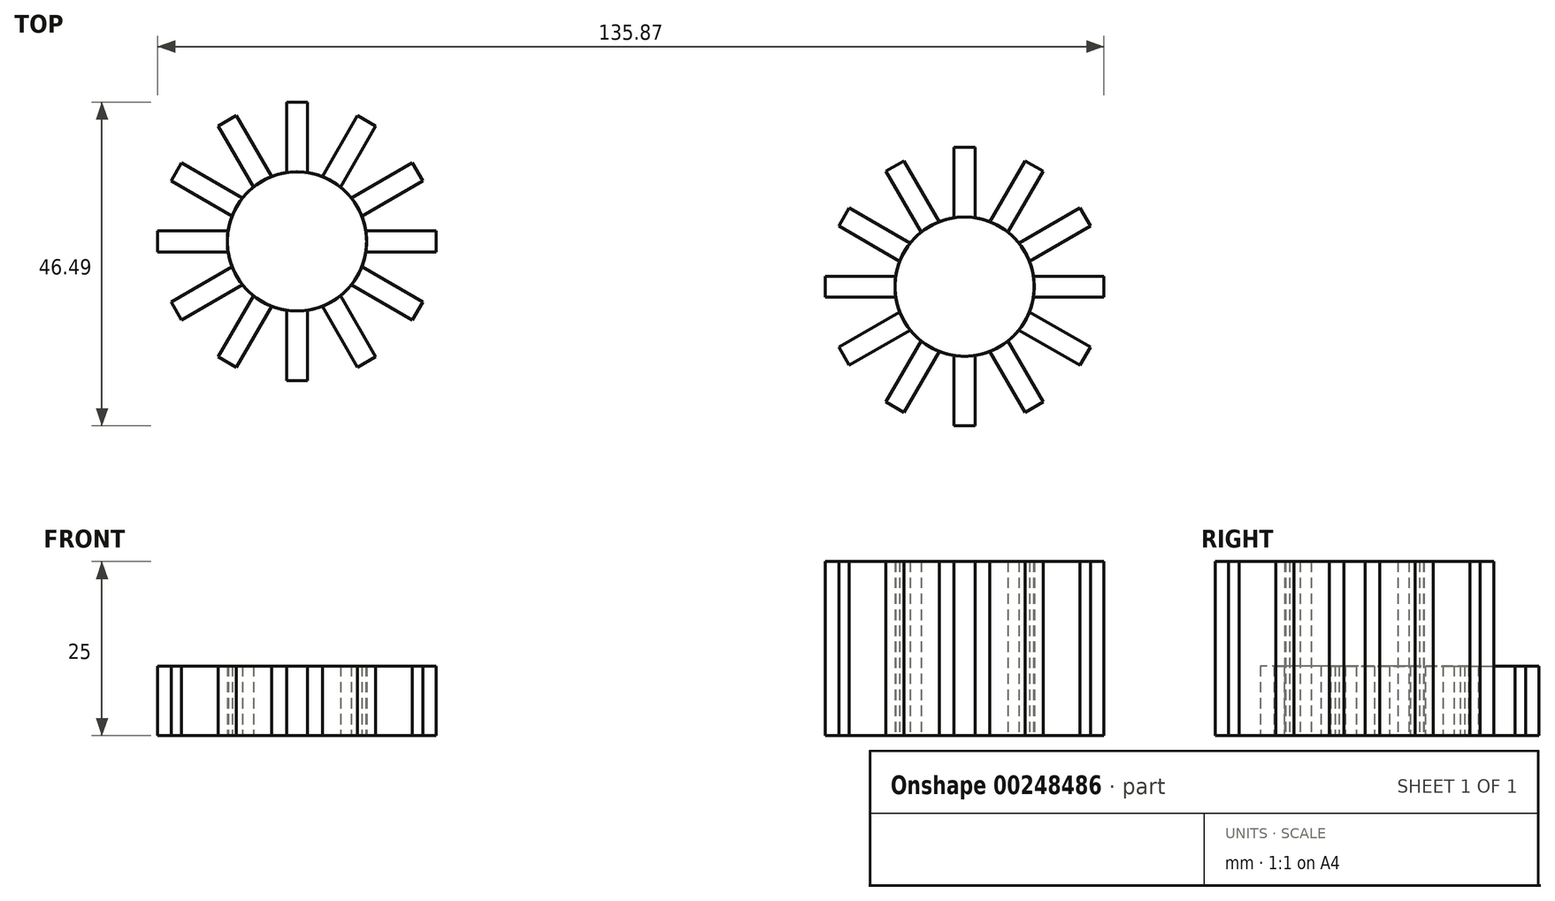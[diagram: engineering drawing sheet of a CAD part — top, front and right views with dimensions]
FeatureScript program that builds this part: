
annotation { "Feature Type Name" : "Feature", "Feature Type Description" : "" }
export const myFeature = defineFeature(function(context is Context, id is Id, definition is map)
    precondition{}
    {
        {
            var Q0;
            Q0=qCreatedBy(makeId("Top.planeOp"),FACE);
            var sketch = newSketch(context, id + "F0", { "sketchPlane" : qUnion([Q0])});
            skCircle(sketch, "E0", {"center": v(0, 0) * mm, "radius": 10 * mm});
            skLineSegment(sketch, "E1", {"start": v(0, 10) * mm, "end": v(0, 15) * mm});
            skLineSegment(sketch, "E2.bottom", {"start": v(1.5, 20) * mm, "end": v(-1.5, 20) * mm});
            skLineSegment(sketch, "E2.left", {"start": v(1.5, 20) * mm, "end": v(1.5, 10) * mm});
            skLineSegment(sketch, "E2.right", {"start": v(-1.5, 20) * mm, "end": v(-1.5, 10) * mm});
            skPoint(sketch, "E2.middle", {"position": v(0, 15) * mm});
            skLineSegment(sketch, "E3", {"start": v(-1.5, 10) * mm, "end": v(-1.5, 9.89) * mm});
            skLineSegment(sketch, "E4", {"start": v(1.5, 10) * mm, "end": v(1.5, 9.89) * mm});
            skSolve(sketch);
        }
        {
            var Q0;
            {var subQ0=sQuery(id+"F0.wireOp",EDGE,"E0");var subQ1=makeQuery(id+"F0.imprint","IMPRINT",VERTEX,{"derivedFrom":subQ0});Q0=makeQuery(id+"F0.imprint","IMPRINT",FACE,{"disambiguationData":[TD([[makeQuery(id+"F0.imprint","IMPRINT",EDGE,{"disambiguationData":[TD([[subQ1,1.0]])],"derivedFrom":subQ0}),1.0]])]});}
            var Q1;
            Q1=makeQuery(id+"F0.imprint","IMPRINT",FACE,{"disambiguationData":[TD([[makeQuery(id+"F0.imprint","IMPRINT",EDGE,{"derivedFrom":sQuery(id+"F0.wireOp",EDGE,"E2.bottom")}),1.0]])]});
            extrude(context, id + "F1", {"entities" : qUnion([Q0, Q1]), "depth" : 25 * mm});
        }
        {
            var Q0;
            Q0=makeQuery(id+"F1.opExtrude","SWEPT_BODY",BODY,{"disambiguationData":[OSD([sQuery(id+"F0.wireOp",EDGE,"E0"),sQuery(id+"F0.wireOp",EDGE,"E2.bottom"),sQuery(id+"F0.wireOp",EDGE,"E2.left"),sQuery(id+"F0.wireOp",EDGE,"E2.right"),sQuery(id+"F0.wireOp",EDGE,"E3"),sQuery(id+"F0.wireOp",EDGE,"E4")])]});
            var Q1;
            Q1=makeQuery(id+"F1.opExtrude","SWEPT_FACE",FACE,{"disambiguationData":[OSD([sQuery(id+"F0.wireOp",EDGE,"E0")])]});
            circularPattern(context, id + "F2", {"entities" : qUnion([Q0]), "axis" : qUnion([Q1]), "angle" : 360 * degree, "instanceCount" : 12, "equalSpace" : true});
        }
        {
            var Q0;
            Q0=qCreatedBy(makeId("Top.planeOp"),FACE);
            var sketch = newSketch(context, id + "F3", { "sketchPlane" : qUnion([Q0])});
            skPoint(sketch, "E5", {"position": v(-95.87, 16.5) * mm});
            skPoint(sketch, "E6", {"position": v(-94.37, 16.5) * mm});
            skPoint(sketch, "E7", {"position": v(-97.37, 16.5) * mm});
            skLineSegment(sketch, "E8.top", {"start": v(-94.37, 26.5) * mm, "end": v(-97.37, 26.5) * mm});
            skLineSegment(sketch, "E8.left", {"start": v(-94.37, 16.5) * mm, "end": v(-94.37, 26.5) * mm});
            skLineSegment(sketch, "E8.right", {"start": v(-97.37, 16.5) * mm, "end": v(-97.37, 26.5) * mm});
            skLineSegment(sketch, "E9", {"start": v(-97.37, 16.5) * mm, "end": v(-97.37, 16.38) * mm});
            skLineSegment(sketch, "E10", {"start": v(-94.37, 16.5) * mm, "end": v(-94.37, 16.38) * mm});
            skPoint(sketch, "E11", {"position": v(-95.87, 6.5) * mm});
            skCircle(sketch, "E12", {"center": v(-95.87, 6.5) * mm, "radius": 10 * mm});
            skSolve(sketch);
        }
        {
            var Q0;
            Q0=makeQuery(id+"F3.imprint","IMPRINT",FACE,{"disambiguationData":[TD([[makeQuery(id+"F3.imprint","IMPRINT",EDGE,{"derivedFrom":sQuery(id+"F3.wireOp",EDGE,"E8.top")}),1.0]])]});
            var Q1;
            {var subQ0=sQuery(id+"F3.wireOp",EDGE,"E12");var subQ1=makeQuery(id+"F3.imprint","INTERSECT",VERTEX,{"derivedFrom":[sQuery(id+"F3.wireOp",EDGE,"E9"),subQ0]});Q1=makeQuery(id+"F3.imprint","IMPRINT",FACE,{"disambiguationData":[TD([[makeQuery(id+"F3.imprint","IMPRINT",EDGE,{"disambiguationData":[TD([[subQ1,1.0]])],"derivedFrom":subQ0}),1.0]])]});}
            extrude(context, id + "F4", {"entities" : qUnion([Q0, Q1]), "depth" : 10 * mm});
        }
        {
            var Q0;
            Q0=makeQuery(id+"F4.opExtrude","SWEPT_BODY",BODY,{"disambiguationData":[OSD([sQuery(id+"F3.wireOp",EDGE,"E8.top"),sQuery(id+"F3.wireOp",EDGE,"E8.left"),sQuery(id+"F3.wireOp",EDGE,"E8.right"),sQuery(id+"F3.wireOp",EDGE,"E9"),sQuery(id+"F3.wireOp",EDGE,"E10"),sQuery(id+"F3.wireOp",EDGE,"E12")])]});
            var Q1;
            Q1=makeQuery(id+"F4.opExtrude","SWEPT_FACE",FACE,{"disambiguationData":[OSD([sQuery(id+"F3.wireOp",EDGE,"E12")])]});
            circularPattern(context, id + "F5", {"entities" : qUnion([Q0]), "axis" : qUnion([Q1]), "angle" : 360 * degree, "instanceCount" : 12, "equalSpace" : true});
        }
    });
